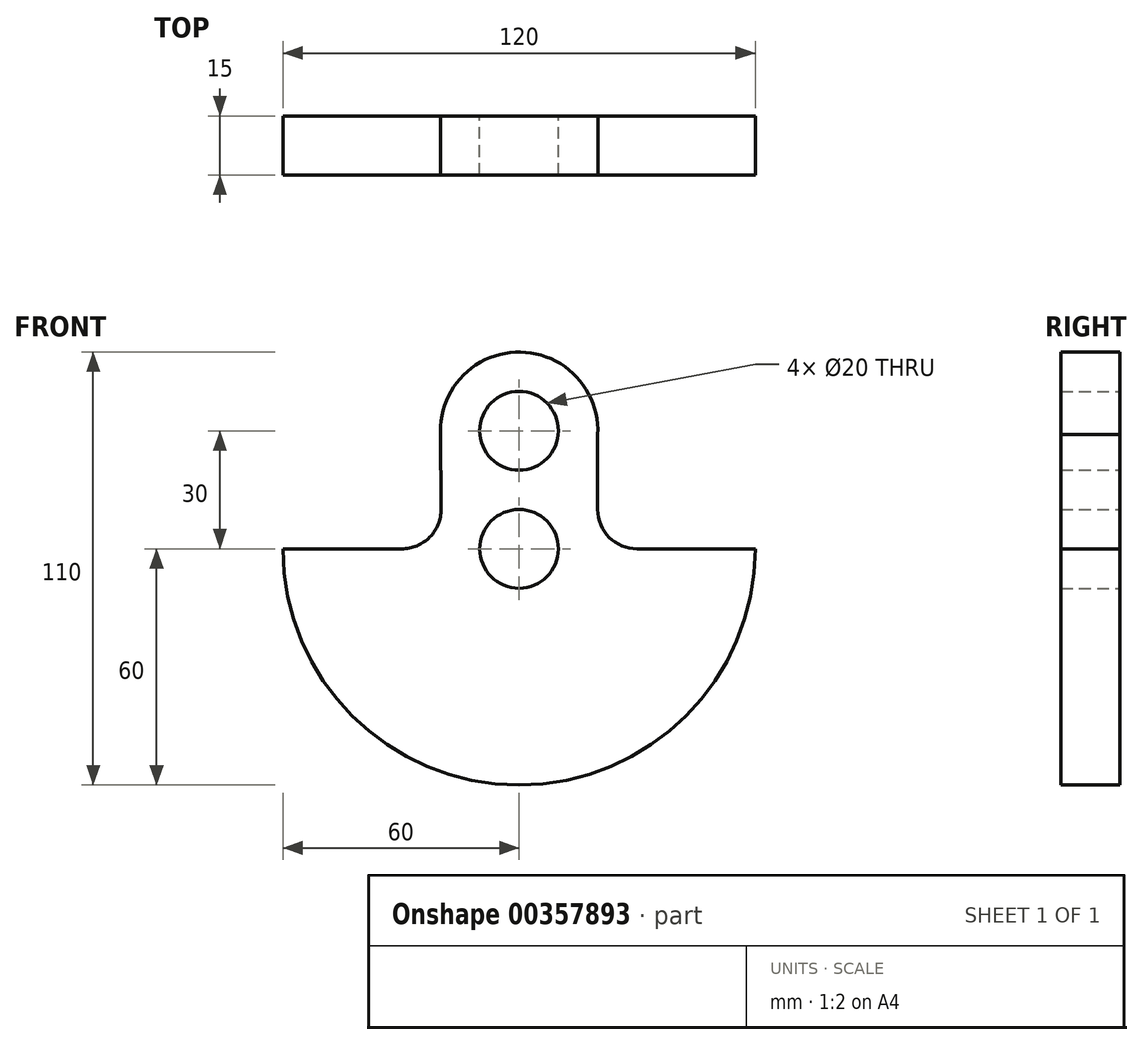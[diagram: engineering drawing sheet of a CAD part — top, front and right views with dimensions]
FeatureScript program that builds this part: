
annotation { "Feature Type Name" : "Feature", "Feature Type Description" : "" }
export const myFeature = defineFeature(function(context is Context, id is Id, definition is map)
    precondition{}
    {
        {
            var Q0;
            Q0=qCreatedBy(makeId("Front.planeOp"),FACE);
            var sketch = newSketch(context, id + "F0", { "sketchPlane" : qUnion([Q0])});
            skArc(sketch, "E0", {"start": v(-60, 0) * mm, "mid": v(0, -60) * mm, "end": v(60, 0) * mm});
            skCircle(sketch, "E1", {"center": v(0, 0) * mm, "radius": 10 * mm});
            skCircle(sketch, "E2", {"center": v(0, 30) * mm, "radius": 10 * mm});
            skArc(sketch, "E3", {"start": v(19.98, 29.06) * mm, "mid": v(0.37, 50) * mm, "end": v(-20, 29.8) * mm});
            skLineSegment(sketch, "E4", {"start": v(-60, 0) * mm, "end": v(-19.7, 0) * mm});
            skLineSegment(sketch, "E5.trimOffspring", {"start": v(19.98, 0) * mm, "end": v(60, 0) * mm});
            skLineSegment(sketch, "E6", {"start": v(-20, 29.8) * mm, "end": v(-19.7, 0) * mm});
            skLineSegment(sketch, "E7", {"start": v(19.98, 29.06) * mm, "end": v(19.98, 0) * mm});
            skSolve(sketch);
        }
        {
            var Q0;
            Q0 = qSketchRegion(id + "F0", true);
            extrude(context, id + "F1", {"entities" : qUnion([Q0]), "depth" : 15 * mm});
        }
        {
            var Q0;
            Q0=makeQuery(id+"F1.opExtrude","SWEPT_EDGE",EDGE,{"disambiguationData":[OSD([sQuery(id+"F0.wireOp",EDGE,"E5.trimOffspring"),sQuery(id+"F0.wireOp",EDGE,"E7")])]});
            fillet(context, id + "F2", {"entities" : qUnion([Q0]), "radius" : 10 * mm, "tangentPropagation" : true, "allowEdgeOverflow" : false});
        }
        {
            var Q0;
            Q0=makeQuery(id+"F1.opExtrude","SWEPT_EDGE",EDGE,{"disambiguationData":[OSD([sQuery(id+"F0.wireOp",EDGE,"E4"),sQuery(id+"F0.wireOp",EDGE,"E6")])]});
            fillet(context, id + "F3", {"entities" : qUnion([Q0]), "radius" : 10 * mm, "tangentPropagation" : true, "allowEdgeOverflow" : false});
        }
    });
